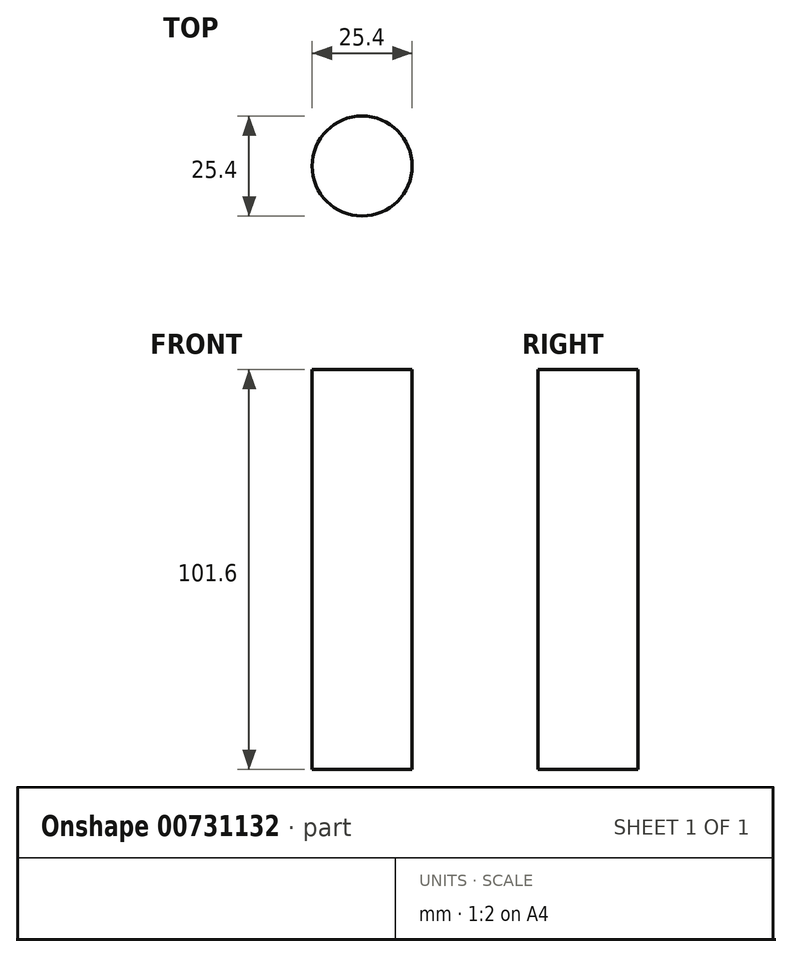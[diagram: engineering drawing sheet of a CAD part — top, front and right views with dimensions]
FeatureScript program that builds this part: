
annotation { "Feature Type Name" : "Feature", "Feature Type Description" : "" }
export const myFeature = defineFeature(function(context is Context, id is Id, definition is map)
    precondition{}
    {
        {
            var Q0;
            Q0=qCreatedBy(makeId("Front.planeOp"),FACE);
            var sketch = newSketch(context, id + "F0", { "sketchPlane" : qUnion([Q0])});
            skLineSegment(sketch, "E0.bottom", {"start": v(-68.71, 89.27) * mm, "end": v(-43.31, 89.27) * mm});
            skLineSegment(sketch, "E0.top", {"start": v(-68.71, -12.33) * mm, "end": v(-43.31, -12.33) * mm});
            skLineSegment(sketch, "E0.left", {"start": v(-68.71, 89.27) * mm, "end": v(-68.71, -12.33) * mm});
            skLineSegment(sketch, "E0.right", {"start": v(-43.31, 89.27) * mm, "end": v(-43.31, -12.33) * mm});
            skLineSegment(sketch, "E1", {"start": v(-56.01, 89.27) * mm, "end": v(-56.01, -12.33) * mm});
            skSolve(sketch);
        }
        {
            var Q0;
            {var subQ0=sQuery(id+"F0.wireOp",EDGE,"E0.right");Q0=makeQuery(id+"F0.imprint","IMPRINT",FACE,{"disambiguationData":[TD([[makeQuery(id+"F0.imprint","IMPRINT",EDGE,{"derivedFrom":subQ0}),-1.0]])]});}
            var Q1;
            Q1=sQuery(id+"F0.wireOp",EDGE,"E1");
            revolve(context, id + "F1", {"surfaceOperationType" : NewSurfaceOperationType.NEW, "entities" : qUnion([Q0]), "axis" : qUnion([Q1]), "revolveType" : RevolveType.FULL});
        }
    });
